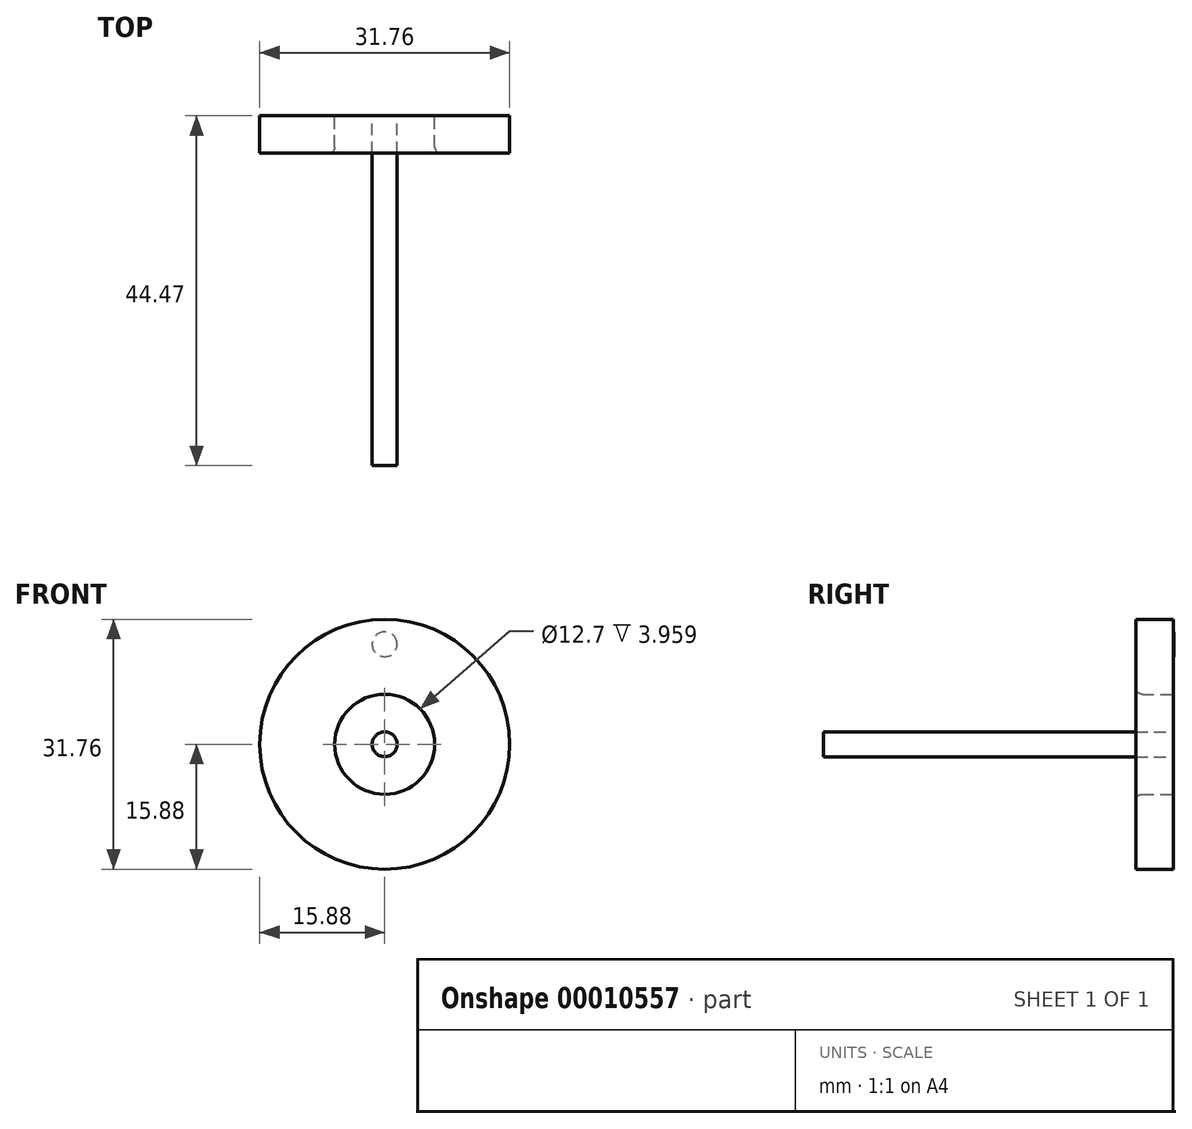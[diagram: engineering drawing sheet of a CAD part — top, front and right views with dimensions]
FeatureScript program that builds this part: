
annotation { "Feature Type Name" : "Feature", "Feature Type Description" : "" }
export const myFeature = defineFeature(function(context is Context, id is Id, definition is map)
    precondition{}
    {
        {
            var Q0;
            Q0=qCreatedBy(makeId("Front.planeOp"),FACE);
            var sketch = newSketch(context, id + "F0", { "sketchPlane" : qUnion([Q0])});
            skCircle(sketch, "E0", {"center": v(0, 0) * mm, "radius": 1.59 * mm});
            skCircle(sketch, "E1", {"center": v(0, 0) * mm, "radius": 6.35 * mm});
            skCircle(sketch, "E2", {"center": v(0, 0) * mm, "radius": 15.88 * mm});
            skCircle(sketch, "E3", {"center": v(0, 0) * mm, "radius": 12.7 * mm, "construction": true});
            skCircle(sketch, "E4", {"center": v(0, 12.7) * mm, "radius": 1.59 * mm});
            skSolve(sketch);
        }
        {
            var Q0;
            Q0=makeQuery(id+"F0.imprint","IMPRINT",FACE,{"disambiguationData":[TD([[makeQuery(id+"F0.imprint","IMPRINT",EDGE,{"derivedFrom":sQuery(id+"F0.wireOp",EDGE,"E1")}),-1.0]])]});
            extrude(context, id + "F1", {"entities" : qUnion([Q0]), "depth" : 4.76 * mm});
        }
        {
            var Q0;
            Q0=makeQuery(id+"F0.imprint","IMPRINT",FACE,{"disambiguationData":[TD([[makeQuery(id+"F0.imprint","IMPRINT",EDGE,{"derivedFrom":sQuery(id+"F0.wireOp",EDGE,"E0")}),-1.0]])]});
            extrude(context, id + "F2", {"entities" : qUnion([Q0]), "operationType" : NewBodyOperationType.ADD, "depth" : 1 / 101.6 * mm});
        }
        {
            var Q0;
            Q0=makeQuery(id+"F0.imprint","IMPRINT",FACE,{"disambiguationData":[TD([[makeQuery(id+"F0.imprint","IMPRINT",EDGE,{"derivedFrom":sQuery(id+"F0.wireOp",EDGE,"E0")}),1.0]])]});
            extrude(context, id + "F3", {"entities" : qUnion([Q0]), "operationType" : NewBodyOperationType.ADD, "depth" : 44.45 * mm});
        }
        {
            var Q0;
            Q0=makeQuery(id+"F1.opExtrude","CAP_EDGE",EDGE,{"disambiguationData":[OSD([sQuery(id+"F0.wireOp",EDGE,"E1")])],"isStart":false});
            fillet(context, id + "F4", {"entities" : qUnion([Q0]), "radius" : 0.8 * mm, "tangentPropagation" : true, "allowEdgeOverflow" : false});
        }
        {
            var Q0;
            Q0=makeQuery(id+"F0.imprint","IMPRINT",FACE,{"disambiguationData":[TD([[makeQuery(id+"F0.imprint","IMPRINT",EDGE,{"derivedFrom":sQuery(id+"F0.wireOp",EDGE,"E4")}),1.0]])]});
            extrude(context, id + "F5", {"entities" : qUnion([Q0]), "oppositeDirection" : true, "depth" : 14.29 * mm, "hasSecondDirection" : true, "secondDirectionOppositeDirection" : false, "secondDirectionDepth" : 3 / 406.4 * mm});
        }
        {
            var Q0;
            Q0=makeQuery(id+"F5.opExtrude","SWEPT_BODY",BODY,{"disambiguationData":[OSD([sQuery(id+"F0.wireOp",EDGE,"E4")])]});
            deleteBodies(context, id + "F6", {"entities" : qUnion([Q0])});
        }
        {
            var Q0;
            Q0=makeQuery(id+"F0.imprint","IMPRINT",FACE,{"disambiguationData":[TD([[makeQuery(id+"F0.imprint","IMPRINT",EDGE,{"derivedFrom":sQuery(id+"F0.wireOp",EDGE,"E4")}),1.0]])]});
            extrude(context, id + "F7", {"entities" : qUnion([Q0]), "operationType" : NewBodyOperationType.ADD, "depth" : 4.76 * mm, "hasSecondDirection" : true, "secondDirectionOppositeDirection" : true, "secondDirectionDepth" : 9 / 406.4 * mm});
        }
    });
